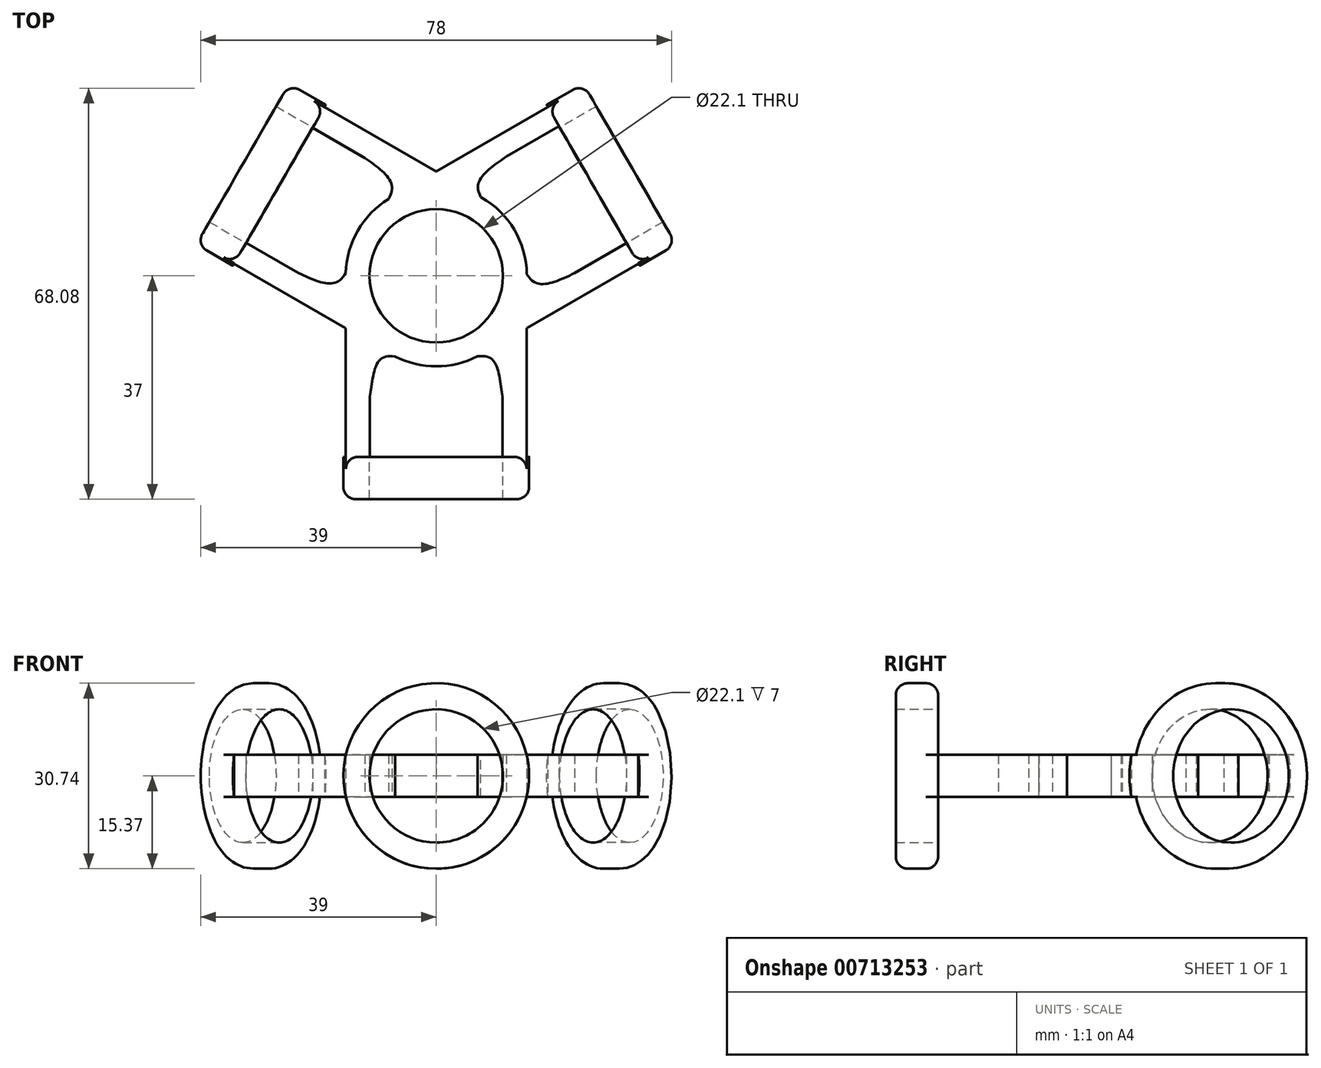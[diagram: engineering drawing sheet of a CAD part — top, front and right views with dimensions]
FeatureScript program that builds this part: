
annotation { "Feature Type Name" : "Feature", "Feature Type Description" : "" }
export const myFeature = defineFeature(function(context is Context, id is Id, definition is map)
    precondition{}
    {
        {
            var Q0;
            Q0=qCreatedBy(makeId("Top.planeOp"),FACE);
            var sketch = newSketch(context, id + "F0", { "sketchPlane" : qUnion([Q0])});
            skCircle(sketch, "E0", {"center": v(0, 0) * mm, "radius": 11.05 * mm});
            skCircle(sketch, "E1", {"center": v(0, 0) * mm, "radius": 15 * mm});
            skLineSegment(sketch, "E2", {"start": v(0, 0) * mm, "end": v(0, -30) * mm, "construction": true});
            skLineSegment(sketch, "E3", {"start": v(0, 0) * mm, "end": v(-25.98, 15) * mm, "construction": true});
            skLineSegment(sketch, "E4", {"start": v(0, 0) * mm, "end": v(25.98, 15) * mm, "construction": true});
            skLineSegment(sketch, "E5", {"start": v(0, 0) * mm, "end": v(7.5, -13) * mm, "construction": true});
            skLineSegment(sketch, "E6", {"start": v(0, -30) * mm, "end": v(-15, -30) * mm, "construction": true});
            skLineSegment(sketch, "E7", {"start": v(0, -30) * mm, "end": v(15, -30) * mm, "construction": true});
            skLineSegment(sketch, "E8", {"start": v(-33.48, 2) * mm, "end": v(-25.98, 15) * mm, "construction": true});
            skLineSegment(sketch, "E9", {"start": v(-18.48, 28) * mm, "end": v(-25.98, 15) * mm, "construction": true});
            skLineSegment(sketch, "E10", {"start": v(18.48, 28) * mm, "end": v(25.98, 15) * mm, "construction": true});
            skLineSegment(sketch, "E11", {"start": v(33.48, 2) * mm, "end": v(25.98, 15) * mm, "construction": true});
            skLineSegment(sketch, "E12", {"start": v(-15, -30) * mm, "end": v(-11, -30) * mm});
            skLineSegment(sketch, "E13", {"start": v(11, -30) * mm, "end": v(15, -30) * mm});
            skLineSegment(sketch, "E14", {"start": v(31.51, 5.42) * mm, "end": v(33.48, 2) * mm});
            skLineSegment(sketch, "E15", {"start": v(18.48, 28) * mm, "end": v(20.33, 24.79) * mm});
            skLineSegment(sketch, "E16", {"start": v(-20.48, 24.53) * mm, "end": v(-18.48, 28) * mm});
            skLineSegment(sketch, "E17", {"start": v(-33.48, 2) * mm, "end": v(-31.48, 5.47) * mm});
            skLineSegment(sketch, "E18", {"start": v(-18.48, 28) * mm, "end": v(7.5, 13) * mm});
            skLineSegment(sketch, "E19", {"start": v(-33.48, 2) * mm, "end": v(-7.5, -13) * mm});
            skLineSegment(sketch, "E20", {"start": v(18.48, 28) * mm, "end": v(-7.5, 13) * mm});
            skLineSegment(sketch, "E21", {"start": v(33.48, 2) * mm, "end": v(7.5, -13) * mm});
            skLineSegment(sketch, "E22", {"start": v(-15, -30) * mm, "end": v(-15, 0) * mm});
            skLineSegment(sketch, "E23", {"start": v(15, -30) * mm, "end": v(15, 0) * mm});
            skLineSegment(sketch, "E24", {"start": v(-11, -30) * mm, "end": v(-11, -10.2) * mm});
            skLineSegment(sketch, "E25", {"start": v(11, -30) * mm, "end": v(11, -10.2) * mm});
            skLineSegment(sketch, "E26", {"start": v(31.51, 5.42) * mm, "end": v(14.3, -4.51) * mm});
            skLineSegment(sketch, "E27", {"start": v(20.33, 24.79) * mm, "end": v(2.9, 14.72) * mm});
            skLineSegment(sketch, "E28", {"start": v(-31.48, 5.47) * mm, "end": v(-14.33, -4.43) * mm});
            skLineSegment(sketch, "E29", {"start": v(-20.48, 24.53) * mm, "end": v(-3.33, 14.63) * mm});
            skLineSegment(sketch, "E30", {"start": v(-22.82, 0.47) * mm, "end": v(-11.82, 19.53) * mm, "construction": true});
            skLineSegment(sketch, "E31", {"start": v(11.61, 19.75) * mm, "end": v(22.9, 0.46) * mm, "construction": true});
            skLineSegment(sketch, "E32", {"start": v(-11, -20) * mm, "end": v(11, -20) * mm, "construction": true});
            skFitSpline(sketch, "E33", {"points": [v(-11, -20) * mm, v(-9, -13.66) * mm, v(0, -15) * mm], "startDerivative": vector(2.85, 13.3) * mm, "endDerivative": vector(18.5, -2.63) * mm});
            skFitSpline(sketch, "E34", {"points": [v(11, -20) * mm, v(9, -13.66) * mm, v(0, -15) * mm], "startDerivative": vector(-2.93, 13.77) * mm, "endDerivative": vector(-18.48, -3.13) * mm});
            skLineSegment(sketch, "E35", {"start": v(-3.33, 14.63) * mm, "end": v(-7.33, 14.63) * mm, "construction": true});
            skLineSegment(sketch, "E36", {"start": v(2.9, 14.72) * mm, "end": v(6.9, 14.72) * mm, "construction": true});
            skLineSegment(sketch, "E37", {"start": v(-11, -10.2) * mm, "end": v(-9, -13.66) * mm, "construction": true});
            skLineSegment(sketch, "E38", {"start": v(0, 0) * mm, "end": v(-7.5, -13) * mm, "construction": true});
            skLineSegment(sketch, "E39", {"start": v(9, -13.66) * mm, "end": v(11, -10.2) * mm, "construction": true});
            skLineSegment(sketch, "E40", {"start": v(0, 0) * mm, "end": v(-7.5, 13) * mm, "construction": true});
            skLineSegment(sketch, "E41", {"start": v(-14.33, -4.43) * mm, "end": v(-16.33, -0.96) * mm, "construction": true});
            skLineSegment(sketch, "E42", {"start": v(14.3, -4.51) * mm, "end": v(16.3, -1.07) * mm, "construction": true});
            skLineSegment(sketch, "E43", {"start": v(-0.13, -0.22) * mm, "end": v(7.5, 13) * mm, "construction": true});
            skFitSpline(sketch, "E44", {"points": [v(-22.82, 0.47) * mm, v(-16.33, -0.96) * mm, v(-13, 7.5) * mm], "startDerivative": vector(15.9, -7.45) * mm, "endDerivative": vector(4.07, 20.77) * mm});
            skFitSpline(sketch, "E45", {"points": [v(-11.82, 19.53) * mm, v(-7.33, 14.63) * mm, v(-13, 7.5) * mm], "startDerivative": vector(14.4, -10.04) * mm, "endDerivative": vector(-15.95, -13.91) * mm});
            skFitSpline(sketch, "E46", {"points": [v(11.61, 19.75) * mm, v(6.9, 14.72) * mm, v(13, 7.5) * mm], "startDerivative": vector(-15.2, -10.36) * mm, "endDerivative": vector(17.12, -14.05) * mm});
            skFitSpline(sketch, "E47", {"points": [v(22.9, 0.46) * mm, v(16.3, -1.07) * mm, v(13, 7.5) * mm], "startDerivative": vector(-16.2, -7.76) * mm, "endDerivative": vector(-3.94, 21.12) * mm});
            skSolve(sketch);
        }
        {
            var Q0;
            Q0 = qSketchRegion(id + "F0", true);
            extrude(context, id + "F1", {"entities" : qUnion([Q0]), "depth" : 7 * mm, "offsetDistance" : 25 * mm});
        }
        {
            var Q0;
            Q0=makeQuery(id+"F1.opExtrude","SWEPT_FACE",FACE,{"disambiguationData":[OSD([sQuery(id+"F0.wireOp",EDGE,"E13")])]});
            var sketch = newSketch(context, id + "F2", { "sketchPlane" : qUnion([Q0])});
            skLineSegment(sketch, "E48", {"start": v(0, 0) * mm, "end": v(0, 3.5) * mm, "construction": true});
            skCircle(sketch, "E49", {"center": v(0, 3.5) * mm, "radius": 11.05 * mm});
            skCircle(sketch, "E50", {"center": v(0, 3.5) * mm, "radius": 15.37 * mm});
            skSolve(sketch);
        }
        {
            var Q0;
            Q0 = qSketchRegion(id + "F2", true);
            extrude(context, id + "F3", {"entities" : qUnion([Q0]), "operationType" : NewBodyOperationType.ADD, "depth" : 7 * mm, "offsetDistance" : 25 * mm});
        }
        {
            var Q0;
            Q0=makeQuery(id+"F1.opExtrude","SWEPT_FACE",FACE,{"disambiguationData":[OSD([sQuery(id+"F0.wireOp",EDGE,"E17")])]});
            var sketch = newSketch(context, id + "F4", { "sketchPlane" : qUnion([Q0])});
            skLineSegment(sketch, "E51", {"start": v(0, 0) * mm, "end": v(0, 3.5) * mm, "construction": true});
            skCircle(sketch, "E52", {"center": v(0, 3.5) * mm, "radius": 11.05 * mm});
            skCircle(sketch, "E53", {"center": v(0, 3.5) * mm, "radius": 15.37 * mm});
            skSolve(sketch);
        }
        {
            var Q0;
            Q0 = qSketchRegion(id + "F4", true);
            extrude(context, id + "F5", {"entities" : qUnion([Q0]), "operationType" : NewBodyOperationType.ADD, "depth" : 7 * mm, "offsetDistance" : 25 * mm});
        }
        {
            var Q0;
            Q0=makeQuery(id+"F1.opExtrude","SWEPT_FACE",FACE,{"disambiguationData":[OSD([sQuery(id+"F0.wireOp",EDGE,"E15")])]});
            var sketch = newSketch(context, id + "F6", { "sketchPlane" : qUnion([Q0])});
            skLineSegment(sketch, "E54", {"start": v(0, 0) * mm, "end": v(0, 3.5) * mm, "construction": true});
            skCircle(sketch, "E55", {"center": v(0, 3.5) * mm, "radius": 11.05 * mm});
            skCircle(sketch, "E56", {"center": v(0, 3.5) * mm, "radius": 15.37 * mm});
            skSolve(sketch);
        }
        {
            var Q0;
            Q0 = qSketchRegion(id + "F6", true);
            extrude(context, id + "F7", {"entities" : qUnion([Q0]), "operationType" : NewBodyOperationType.ADD, "depth" : 7 * mm, "offsetDistance" : 25 * mm});
        }
        {
            var Q0;
            {var subQ0=sQuery(id+"F0.wireOp",EDGE,"M36BIH5r-HAUe-k9cw-Y8AN-n1bEUGcGn69A");Q0=makeQuery(id+"F1.opExtrude","CAP_EDGE",EDGE,{"disambiguationData":[OSD([subQ0]),TDD([makeQuery(id+"F0.imprint","IMPRINT",EDGE,{"disambiguationData":[TD([[makeQuery(id+"F0.imprint","INTERSECT",VERTEX,{"derivedFrom":[subQ0,sQuery(id+"F0.wireOp",EDGE,"E17")]}),-1.0]])],"derivedFrom":subQ0})])],"isStart":false});}
            var Q1;
            {var subQ0=sQuery(id+"F0.wireOp",EDGE,"BCidmaKO-JP6u-Ivkp-FLMH-IQCRB2LKm121");Q1=makeQuery(id+"F1.opExtrude","CAP_EDGE",EDGE,{"disambiguationData":[OSD([subQ0]),TDD([makeQuery(id+"F0.imprint","IMPRINT",EDGE,{"disambiguationData":[TD([[makeQuery(id+"F0.imprint","INTERSECT",VERTEX,{"derivedFrom":[subQ0,sQuery(id+"F0.wireOp",EDGE,"E16")]}),-1.0]])],"derivedFrom":subQ0})])],"isStart":false});}
            var Q2;
            {var subQ0=sQuery(id+"F0.wireOp",EDGE,"lp6IFI2F-ik4T-MF6x-9fN9-Xrn4K0irZbfQ");Q2=makeQuery(id+"F1.opExtrude","CAP_EDGE",EDGE,{"disambiguationData":[OSD([subQ0]),TDD([makeQuery(id+"F0.imprint","IMPRINT",EDGE,{"disambiguationData":[TD([[makeQuery(id+"F0.imprint","INTERSECT",VERTEX,{"derivedFrom":[subQ0,sQuery(id+"F0.wireOp",EDGE,"E15")]}),-1.0]])],"derivedFrom":subQ0})])],"isStart":false});}
            var Q3;
            {var subQ0=sQuery(id+"F0.wireOp",EDGE,"ELQnSAp0-Pafx-ul33-bJbq-gA5hsUOoMWmb");Q3=makeQuery(id+"F1.opExtrude","CAP_EDGE",EDGE,{"disambiguationData":[OSD([subQ0]),TDD([makeQuery(id+"F0.imprint","IMPRINT",EDGE,{"disambiguationData":[TD([[makeQuery(id+"F0.imprint","INTERSECT",VERTEX,{"derivedFrom":[subQ0,sQuery(id+"F0.wireOp",EDGE,"E14")]}),-1.0]])],"derivedFrom":subQ0})])],"isStart":false});}
            var Q4;
            {var subQ0=sQuery(id+"F0.wireOp",EDGE,"Rb86YKMy-m54r-hE0W-wiJ9-LWPDYXBjSwaC");Q4=makeQuery(id+"F1.opExtrude","CAP_EDGE",EDGE,{"disambiguationData":[OSD([subQ0]),TDD([makeQuery(id+"F0.imprint","IMPRINT",EDGE,{"disambiguationData":[TD([[makeQuery(id+"F0.imprint","INTERSECT",VERTEX,{"derivedFrom":[subQ0,sQuery(id+"F0.wireOp",EDGE,"E13")]}),-1.0]])],"derivedFrom":subQ0})])],"isStart":false});}
            var Q5;
            {var subQ0=sQuery(id+"F0.wireOp",EDGE,"FxYZINIX-OOwV-yyRV-FRkK-c2HcUoVdKEcg");Q5=makeQuery(id+"F1.opExtrude","CAP_EDGE",EDGE,{"disambiguationData":[OSD([subQ0]),TDD([makeQuery(id+"F0.imprint","IMPRINT",EDGE,{"disambiguationData":[TD([[makeQuery(id+"F0.imprint","INTERSECT",VERTEX,{"derivedFrom":[subQ0,sQuery(id+"F0.wireOp",EDGE,"E12")]}),-1.0]])],"derivedFrom":subQ0})])],"isStart":false});}
            var Q6;
            {var subQ0=sQuery(id+"F0.wireOp",EDGE,"Rb86YKMy-m54r-hE0W-wiJ9-LWPDYXBjSwaC");Q6=makeQuery(id+"F1.opExtrude","CAP_EDGE",EDGE,{"disambiguationData":[OSD([subQ0]),TDD([makeQuery(id+"F0.imprint","IMPRINT",EDGE,{"disambiguationData":[TD([[makeQuery(id+"F0.imprint","INTERSECT",VERTEX,{"derivedFrom":[subQ0,sQuery(id+"F0.wireOp",EDGE,"E13")]}),-1.0]])],"derivedFrom":subQ0})])],"isStart":true});}
            var Q7;
            {var subQ0=sQuery(id+"F0.wireOp",EDGE,"ELQnSAp0-Pafx-ul33-bJbq-gA5hsUOoMWmb");Q7=makeQuery(id+"F1.opExtrude","CAP_EDGE",EDGE,{"disambiguationData":[OSD([subQ0]),TDD([makeQuery(id+"F0.imprint","IMPRINT",EDGE,{"disambiguationData":[TD([[makeQuery(id+"F0.imprint","INTERSECT",VERTEX,{"derivedFrom":[subQ0,sQuery(id+"F0.wireOp",EDGE,"E14")]}),-1.0]])],"derivedFrom":subQ0})])],"isStart":true});}
            var Q8;
            {var subQ0=sQuery(id+"F0.wireOp",EDGE,"lp6IFI2F-ik4T-MF6x-9fN9-Xrn4K0irZbfQ");Q8=makeQuery(id+"F1.opExtrude","CAP_EDGE",EDGE,{"disambiguationData":[OSD([subQ0]),TDD([makeQuery(id+"F0.imprint","IMPRINT",EDGE,{"disambiguationData":[TD([[makeQuery(id+"F0.imprint","INTERSECT",VERTEX,{"derivedFrom":[subQ0,sQuery(id+"F0.wireOp",EDGE,"E15")]}),-1.0]])],"derivedFrom":subQ0})])],"isStart":true});}
            var Q9;
            {var subQ0=sQuery(id+"F0.wireOp",EDGE,"BCidmaKO-JP6u-Ivkp-FLMH-IQCRB2LKm121");Q9=makeQuery(id+"F1.opExtrude","CAP_EDGE",EDGE,{"disambiguationData":[OSD([subQ0]),TDD([makeQuery(id+"F0.imprint","IMPRINT",EDGE,{"disambiguationData":[TD([[makeQuery(id+"F0.imprint","INTERSECT",VERTEX,{"derivedFrom":[subQ0,sQuery(id+"F0.wireOp",EDGE,"E16")]}),-1.0]])],"derivedFrom":subQ0})])],"isStart":true});}
            var Q10;
            {var subQ0=sQuery(id+"F0.wireOp",EDGE,"M36BIH5r-HAUe-k9cw-Y8AN-n1bEUGcGn69A");Q10=makeQuery(id+"F1.opExtrude","CAP_EDGE",EDGE,{"disambiguationData":[OSD([subQ0]),TDD([makeQuery(id+"F0.imprint","IMPRINT",EDGE,{"disambiguationData":[TD([[makeQuery(id+"F0.imprint","INTERSECT",VERTEX,{"derivedFrom":[subQ0,sQuery(id+"F0.wireOp",EDGE,"E17")]}),-1.0]])],"derivedFrom":subQ0})])],"isStart":true});}
            var Q11;
            {var subQ0=sQuery(id+"F0.wireOp",EDGE,"FxYZINIX-OOwV-yyRV-FRkK-c2HcUoVdKEcg");Q11=makeQuery(id+"F1.opExtrude","CAP_EDGE",EDGE,{"disambiguationData":[OSD([subQ0]),TDD([makeQuery(id+"F0.imprint","IMPRINT",EDGE,{"disambiguationData":[TD([[makeQuery(id+"F0.imprint","INTERSECT",VERTEX,{"derivedFrom":[subQ0,sQuery(id+"F0.wireOp",EDGE,"E12")]}),-1.0]])],"derivedFrom":subQ0})])],"isStart":true});}
            var Q12;
            Q12=makeQuery(id+"F7.opExtrude","CAP_EDGE",EDGE,{"disambiguationData":[OSD([sQuery(id+"F6.wireOp",EDGE,"E56")])],"isStart":false});
            var Q13;
            Q13=makeQuery(id+"F3.opExtrude","CAP_EDGE",EDGE,{"disambiguationData":[OSD([sQuery(id+"F2.wireOp",EDGE,"E50")])],"isStart":false});
            var Q14;
            Q14=makeQuery(id+"F5.opExtrude","CAP_EDGE",EDGE,{"disambiguationData":[OSD([sQuery(id+"F4.wireOp",EDGE,"E53")])],"isStart":false});
            fillet(context, id + "F8", {"entities" : qUnion([Q0, Q1, Q2, Q3, Q4, Q5, Q6, Q7, Q8, Q9, Q10, Q11, Q12, Q13, Q14]), "radius" : 2 * mm, "tangentPropagation" : true, "allowEdgeOverflow" : false});
        }
        {
            var Q0;
            {var subQ0=sQuery(id+"F0.wireOp",EDGE,"E13");var subQ2=sQuery(id+"F2.wireOp",EDGE,"E50");var subQ3=makeQuery(id+"F3.opExtrude","CAP_FACE",FACE,{"disambiguationData":[OSD([sQuery(id+"F2.wireOp",EDGE,"E49"),subQ2])],"isStart":true});var subQ4=sQuery(id+"F0.wireOp",EDGE,"E12");var subQ6=sQuery(id+"F0.wireOp",EDGE,"E17");var subQ7=sQuery(id+"F0.wireOp",EDGE,"E16");var subQ8=sQuery(id+"F0.wireOp",EDGE,"E15");var subQ9=sQuery(id+"F0.wireOp",EDGE,"E14");var subQ10=sQuery(id+"F0.wireOp",EDGE,"yFMh2vSi-dESU-roSY-NlWJ-D2NnP62kJ6aZ");var subQ11=sQuery(id+"F0.wireOp",EDGE,"MxBJSyvS-Fmrp-042r-ySUE-HMpYeUpcr8Ry");var subQ12=sQuery(id+"F0.wireOp",EDGE,"cHBSjouM-ive9-fqb4-oQAG-pubF9SUR5cwU");var subQ13=sQuery(id+"F0.wireOp",EDGE,"rupdORs6-A4il-8cmi-DNMe-a3LxSKAeor8D");var subQ14=sQuery(id+"F0.wireOp",EDGE,"dYG0iTOq-gft9-4OFM-1PV2-ACBu23Gv7qJD");var subQ15=sQuery(id+"F0.wireOp",EDGE,"M8sEbQj8-NoZn-PTSG-Y4XU-dObeHGLnaSbQ");var subQ16=sQuery(id+"F0.wireOp",EDGE,"lp6IFI2F-ik4T-MF6x-9fN9-Xrn4K0irZbfQ");var subQ17=sQuery(id+"F0.wireOp",EDGE,"BCidmaKO-JP6u-Ivkp-FLMH-IQCRB2LKm121");var subQ18=sQuery(id+"F0.wireOp",EDGE,"ELQnSAp0-Pafx-ul33-bJbq-gA5hsUOoMWmb");var subQ19=sQuery(id+"F0.wireOp",EDGE,"Rb86YKMy-m54r-hE0W-wiJ9-LWPDYXBjSwaC");var subQ20=sQuery(id+"F0.wireOp",EDGE,"FxYZINIX-OOwV-yyRV-FRkK-c2HcUoVdKEcg");var subQ21=sQuery(id+"F0.wireOp",EDGE,"M36BIH5r-HAUe-k9cw-Y8AN-n1bEUGcGn69A");var subQ22=sQuery(id+"F0.wireOp",EDGE,"E1");var subQ23=sQuery(id+"F0.wireOp",EDGE,"E0");var subQ24=makeQuery(id+"F3.opExtrude","SWEPT_FACE",FACE,{"disambiguationData":[OSD([subQ2])]});var subQ25=makeQuery(id+"F3.opExtrude","CAP_EDGE",EDGE,{"disambiguationData":[OSD([subQ2])],"isStart":true});Q0=makeQuery(id+"F8.opFillet","MERGE",EDGE,{"derivedFrom":[makeQuery(id+"F3.boolean.opBoolean","SPLIT",EDGE,{"disambiguationData":[topologyDisambiguationEdgeConnected([subQ3,subQ24]),TD([makeQuery(id+"F1.opExtrude","SWEPT_FACE",FACE,{"disambiguationData":[OSD([subQ20]),TDD([makeQuery(id+"F0.imprint","IMPRINT",EDGE,{"disambiguationData":[TD([[makeQuery(id+"F0.imprint","INTERSECT",VERTEX,{"derivedFrom":[subQ20,subQ4]}),-1.0]])],"derivedFrom":subQ20})])]})])],"derivedFrom":subQ25}),makeQuery(id+"F3.boolean.opBoolean","SPLIT",EDGE,{"disambiguationData":[topologyDisambiguationEdgeConnected([subQ3,subQ24]),TD([makeQuery(id+"F1.opExtrude","SWEPT_FACE",FACE,{"disambiguationData":[OSD([subQ19]),TDD([makeQuery(id+"F0.imprint","IMPRINT",EDGE,{"disambiguationData":[TD([[makeQuery(id+"F0.imprint","INTERSECT",VERTEX,{"derivedFrom":[subQ19,subQ0]}),-1.0]])],"derivedFrom":subQ19})])]})])],"derivedFrom":subQ25}),makeQuery(id+"F3.boolean.opBoolean","SPLIT",EDGE,{"disambiguationData":[topologyDisambiguationEdgeConnected([subQ3,subQ24]),TD([makeQuery(id+"F1.opExtrude","CAP_FACE",FACE,{"disambiguationData":[OSD([subQ23,subQ22,subQ21,subQ20,subQ19,subQ18,subQ17,subQ16,subQ15,subQ14,subQ13,subQ12,subQ11,subQ10,subQ4,subQ0,subQ9,subQ8,subQ7,subQ6])],"isStart":true})])],"derivedFrom":subQ25}),makeQuery(id+"F3.boolean.opBoolean","SPLIT",EDGE,{"disambiguationData":[topologyDisambiguationEdgeConnected([subQ3,subQ24]),TD([makeQuery(id+"F1.opExtrude","CAP_FACE",FACE,{"disambiguationData":[OSD([subQ23,subQ22,subQ21,subQ20,subQ19,subQ18,subQ17,subQ16,subQ15,subQ14,subQ13,subQ12,subQ11,subQ10,subQ4,subQ0,subQ9,subQ8,subQ7,subQ6])],"isStart":false})])],"derivedFrom":subQ25})]});}
            var Q1;
            {var subQ0=sQuery(id+"F0.wireOp",EDGE,"E14");var subQ2=sQuery(id+"F6.wireOp",EDGE,"E56");var subQ3=makeQuery(id+"F7.opExtrude","CAP_FACE",FACE,{"disambiguationData":[OSD([sQuery(id+"F6.wireOp",EDGE,"E55"),subQ2])],"isStart":true});var subQ4=sQuery(id+"F0.wireOp",EDGE,"E15");var subQ6=sQuery(id+"F0.wireOp",EDGE,"E17");var subQ7=sQuery(id+"F0.wireOp",EDGE,"E16");var subQ8=sQuery(id+"F0.wireOp",EDGE,"E13");var subQ9=sQuery(id+"F0.wireOp",EDGE,"E12");var subQ10=sQuery(id+"F0.wireOp",EDGE,"yFMh2vSi-dESU-roSY-NlWJ-D2NnP62kJ6aZ");var subQ11=sQuery(id+"F0.wireOp",EDGE,"MxBJSyvS-Fmrp-042r-ySUE-HMpYeUpcr8Ry");var subQ12=sQuery(id+"F0.wireOp",EDGE,"cHBSjouM-ive9-fqb4-oQAG-pubF9SUR5cwU");var subQ13=sQuery(id+"F0.wireOp",EDGE,"rupdORs6-A4il-8cmi-DNMe-a3LxSKAeor8D");var subQ14=sQuery(id+"F0.wireOp",EDGE,"dYG0iTOq-gft9-4OFM-1PV2-ACBu23Gv7qJD");var subQ15=sQuery(id+"F0.wireOp",EDGE,"M8sEbQj8-NoZn-PTSG-Y4XU-dObeHGLnaSbQ");var subQ16=sQuery(id+"F0.wireOp",EDGE,"lp6IFI2F-ik4T-MF6x-9fN9-Xrn4K0irZbfQ");var subQ17=sQuery(id+"F0.wireOp",EDGE,"BCidmaKO-JP6u-Ivkp-FLMH-IQCRB2LKm121");var subQ18=sQuery(id+"F0.wireOp",EDGE,"ELQnSAp0-Pafx-ul33-bJbq-gA5hsUOoMWmb");var subQ19=sQuery(id+"F0.wireOp",EDGE,"Rb86YKMy-m54r-hE0W-wiJ9-LWPDYXBjSwaC");var subQ20=sQuery(id+"F0.wireOp",EDGE,"FxYZINIX-OOwV-yyRV-FRkK-c2HcUoVdKEcg");var subQ21=sQuery(id+"F0.wireOp",EDGE,"M36BIH5r-HAUe-k9cw-Y8AN-n1bEUGcGn69A");var subQ22=sQuery(id+"F0.wireOp",EDGE,"E1");var subQ23=sQuery(id+"F0.wireOp",EDGE,"E0");var subQ24=makeQuery(id+"F7.opExtrude","SWEPT_FACE",FACE,{"disambiguationData":[OSD([subQ2])]});var subQ25=makeQuery(id+"F7.opExtrude","CAP_EDGE",EDGE,{"disambiguationData":[OSD([subQ2])],"isStart":true});Q1=makeQuery(id+"F8.opFillet","MERGE",EDGE,{"derivedFrom":[makeQuery(id+"F7.boolean.opBoolean","SPLIT",EDGE,{"disambiguationData":[topologyDisambiguationEdgeConnected([subQ3,subQ24]),TD([makeQuery(id+"F1.opExtrude","SWEPT_FACE",FACE,{"disambiguationData":[OSD([subQ18]),TDD([makeQuery(id+"F0.imprint","IMPRINT",EDGE,{"disambiguationData":[TD([[makeQuery(id+"F0.imprint","INTERSECT",VERTEX,{"derivedFrom":[subQ18,subQ0]}),-1.0]])],"derivedFrom":subQ18})])]})])],"derivedFrom":subQ25}),makeQuery(id+"F7.boolean.opBoolean","SPLIT",EDGE,{"disambiguationData":[topologyDisambiguationEdgeConnected([subQ3,subQ24]),TD([makeQuery(id+"F1.opExtrude","SWEPT_FACE",FACE,{"disambiguationData":[OSD([subQ16]),TDD([makeQuery(id+"F0.imprint","IMPRINT",EDGE,{"disambiguationData":[TD([[makeQuery(id+"F0.imprint","INTERSECT",VERTEX,{"derivedFrom":[subQ16,subQ4]}),-1.0]])],"derivedFrom":subQ16})])]})])],"derivedFrom":subQ25}),makeQuery(id+"F7.boolean.opBoolean","SPLIT",EDGE,{"disambiguationData":[topologyDisambiguationEdgeConnected([subQ3,subQ24]),TD([makeQuery(id+"F1.opExtrude","CAP_FACE",FACE,{"disambiguationData":[OSD([subQ23,subQ22,subQ21,subQ20,subQ19,subQ18,subQ17,subQ16,subQ15,subQ14,subQ13,subQ12,subQ11,subQ10,subQ9,subQ8,subQ0,subQ4,subQ7,subQ6])],"isStart":true})])],"derivedFrom":subQ25}),makeQuery(id+"F7.boolean.opBoolean","SPLIT",EDGE,{"disambiguationData":[topologyDisambiguationEdgeConnected([subQ3,subQ24]),TD([makeQuery(id+"F1.opExtrude","CAP_FACE",FACE,{"disambiguationData":[OSD([subQ23,subQ22,subQ21,subQ20,subQ19,subQ18,subQ17,subQ16,subQ15,subQ14,subQ13,subQ12,subQ11,subQ10,subQ9,subQ8,subQ0,subQ4,subQ7,subQ6])],"isStart":false})])],"derivedFrom":subQ25})]});}
            fillet(context, id + "F9", {"entities" : qUnion([Q0, Q1]), "radius" : 2 * mm, "tangentPropagation" : true, "allowEdgeOverflow" : false});
        }
        {
            var Q0;
            {var subQ0=sQuery(id+"F4.wireOp",EDGE,"E53");var subQ1=makeQuery(id+"F5.opExtrude","CAP_FACE",FACE,{"disambiguationData":[OSD([sQuery(id+"F4.wireOp",EDGE,"E52"),subQ0])],"isStart":true});var subQ2=sQuery(id+"F0.wireOp",EDGE,"E16");var subQ3=sQuery(id+"F0.wireOp",EDGE,"E17");var subQ4=makeQuery(id+"F5.opExtrude","SWEPT_FACE",FACE,{"disambiguationData":[OSD([subQ0])]});Q0=makeQuery(id+"F5.boolean.opBoolean","SPLIT",EDGE,{"disambiguationData":[topologyDisambiguationEdgeConnected([subQ1,subQ4]),TD([makeQuery(id+"F1.opExtrude","CAP_FACE",FACE,{"disambiguationData":[OSD([sQuery(id+"F0.wireOp",EDGE,"E0"),sQuery(id+"F0.wireOp",EDGE,"E1"),sQuery(id+"F0.wireOp",EDGE,"E12"),sQuery(id+"F0.wireOp",EDGE,"E13"),sQuery(id+"F0.wireOp",EDGE,"E14"),sQuery(id+"F0.wireOp",EDGE,"E15"),subQ2,subQ3,sQuery(id+"F0.wireOp",EDGE,"E18"),sQuery(id+"F0.wireOp",EDGE,"E19"),sQuery(id+"F0.wireOp",EDGE,"E20"),sQuery(id+"F0.wireOp",EDGE,"E21"),sQuery(id+"F0.wireOp",EDGE,"E22"),sQuery(id+"F0.wireOp",EDGE,"E23"),sQuery(id+"F0.wireOp",EDGE,"E24"),sQuery(id+"F0.wireOp",EDGE,"E25"),sQuery(id+"F0.wireOp",EDGE,"E26"),sQuery(id+"F0.wireOp",EDGE,"E27"),sQuery(id+"F0.wireOp",EDGE,"E28"),sQuery(id+"F0.wireOp",EDGE,"E29")])],"isStart":true})])],"derivedFrom":makeQuery(id+"F5.opExtrude","CAP_EDGE",EDGE,{"disambiguationData":[OSD([subQ0])],"isStart":true})});}
            var Q1;
            {var subQ0=sQuery(id+"F4.wireOp",EDGE,"E53");var subQ1=makeQuery(id+"F5.opExtrude","CAP_FACE",FACE,{"disambiguationData":[OSD([sQuery(id+"F4.wireOp",EDGE,"E52"),subQ0])],"isStart":true});var subQ2=sQuery(id+"F0.wireOp",EDGE,"E17");var subQ3=sQuery(id+"F0.wireOp",EDGE,"E16");var subQ4=makeQuery(id+"F5.opExtrude","SWEPT_FACE",FACE,{"disambiguationData":[OSD([subQ0])]});Q1=makeQuery(id+"F5.boolean.opBoolean","SPLIT",EDGE,{"disambiguationData":[topologyDisambiguationEdgeConnected([subQ1,subQ4]),TD([makeQuery(id+"F1.opExtrude","CAP_FACE",FACE,{"disambiguationData":[OSD([sQuery(id+"F0.wireOp",EDGE,"E0"),sQuery(id+"F0.wireOp",EDGE,"E1"),sQuery(id+"F0.wireOp",EDGE,"E12"),sQuery(id+"F0.wireOp",EDGE,"E13"),sQuery(id+"F0.wireOp",EDGE,"E14"),sQuery(id+"F0.wireOp",EDGE,"E15"),subQ3,subQ2,sQuery(id+"F0.wireOp",EDGE,"E18"),sQuery(id+"F0.wireOp",EDGE,"E19"),sQuery(id+"F0.wireOp",EDGE,"E20"),sQuery(id+"F0.wireOp",EDGE,"E21"),sQuery(id+"F0.wireOp",EDGE,"E22"),sQuery(id+"F0.wireOp",EDGE,"E23"),sQuery(id+"F0.wireOp",EDGE,"E24"),sQuery(id+"F0.wireOp",EDGE,"E25"),sQuery(id+"F0.wireOp",EDGE,"E26"),sQuery(id+"F0.wireOp",EDGE,"E27"),sQuery(id+"F0.wireOp",EDGE,"E28"),sQuery(id+"F0.wireOp",EDGE,"E29")])],"isStart":false})])],"derivedFrom":makeQuery(id+"F5.opExtrude","CAP_EDGE",EDGE,{"disambiguationData":[OSD([subQ0])],"isStart":true})});}
            fillet(context, id + "F10", {"entities" : qUnion([Q0, Q1]), "radius" : 2 * mm, "tangentPropagation" : true, "allowEdgeOverflow" : false});
        }
        {
            var Q0;
            {var subQ0=sQuery(id+"F0.wireOp",EDGE,"E19");var subQ1=sQuery(id+"F0.wireOp",EDGE,"E1");var subQ2=makeQuery(id+"F0.imprint","INTERSECT",VERTEX,{"derivedFrom":[subQ1,subQ0]});Q0=makeQuery(id+"F0.imprint","IMPRINT",FACE,{"disambiguationData":[TD([[makeQuery(id+"F0.imprint","IMPRINT",EDGE,{"disambiguationData":[TD([[subQ2,1.0]])],"derivedFrom":subQ1}),-1.0]])]});}
            extrude(context, id + "F11", {"entities" : qUnion([Q0]), "operationType" : NewBodyOperationType.ADD, "depth" : 7 * mm, "offsetDistance" : 25 * mm});
        }
        {
            var Q0;
            {var subQ0=sQuery(id+"F0.wireOp",EDGE,"E21");var subQ1=sQuery(id+"F0.wireOp",EDGE,"E1");var subQ2=makeQuery(id+"F0.imprint","INTERSECT",VERTEX,{"derivedFrom":[subQ1,subQ0]});Q0=makeQuery(id+"F0.imprint","IMPRINT",FACE,{"disambiguationData":[TD([[makeQuery(id+"F0.imprint","IMPRINT",EDGE,{"disambiguationData":[TD([[subQ2,-1.0]])],"derivedFrom":subQ1}),-1.0]])]});}
            extrude(context, id + "F12", {"entities" : qUnion([Q0]), "operationType" : NewBodyOperationType.ADD, "depth" : 7 * mm, "offsetDistance" : 25 * mm});
        }
        {
            var Q0;
            {var subQ0=sQuery(id+"F0.wireOp",EDGE,"E22");var subQ1=sQuery(id+"F0.wireOp",EDGE,"E1");var subQ2=makeQuery(id+"F0.imprint","INTERSECT",VERTEX,{"derivedFrom":[subQ1,subQ0]});Q0=makeQuery(id+"F0.imprint","IMPRINT",FACE,{"disambiguationData":[TD([[makeQuery(id+"F0.imprint","IMPRINT",EDGE,{"disambiguationData":[TD([[subQ2,-1.0]])],"derivedFrom":subQ1}),-1.0]])]});}
            extrude(context, id + "F13", {"entities" : qUnion([Q0]), "operationType" : NewBodyOperationType.ADD, "depth" : 7 * mm, "offsetDistance" : 25 * mm});
        }
        {
            var Q0;
            {var subQ0=sQuery(id+"F0.wireOp",EDGE,"E21");var subQ1=sQuery(id+"F0.wireOp",EDGE,"E1");var subQ2=makeQuery(id+"F0.imprint","INTERSECT",VERTEX,{"derivedFrom":[subQ1,subQ0]});Q0=makeQuery(id+"F0.imprint","IMPRINT",FACE,{"disambiguationData":[TD([[makeQuery(id+"F0.imprint","IMPRINT",EDGE,{"disambiguationData":[TD([[subQ2,-1.0]])],"derivedFrom":subQ1}),-1.0]])]});}
            var Q1;
            {var subQ0=sQuery(id+"F0.wireOp",EDGE,"E23");var subQ1=sQuery(id+"F0.wireOp",EDGE,"E1");var subQ2=makeQuery(id+"F0.imprint","INTERSECT",VERTEX,{"derivedFrom":[subQ1,subQ0]});Q1=makeQuery(id+"F0.imprint","IMPRINT",FACE,{"disambiguationData":[TD([[makeQuery(id+"F0.imprint","IMPRINT",EDGE,{"disambiguationData":[TD([[subQ2,1.0]])],"derivedFrom":subQ1}),-1.0]])]});}
            var Q2;
            {var subQ0=sQuery(id+"F0.wireOp",EDGE,"E27");var subQ1=sQuery(id+"F0.wireOp",EDGE,"E1");var subQ2=makeQuery(id+"F0.imprint","INTERSECT",VERTEX,{"derivedFrom":[subQ1,subQ0]});Q2=makeQuery(id+"F0.imprint","IMPRINT",FACE,{"disambiguationData":[TD([[makeQuery(id+"F0.imprint","IMPRINT",EDGE,{"disambiguationData":[TD([[subQ2,1.0]])],"derivedFrom":subQ1}),-1.0]])]});}
            var Q3;
            {var subQ0=sQuery(id+"F0.wireOp",EDGE,"E20");var subQ1=sQuery(id+"F0.wireOp",EDGE,"E1");var subQ2=makeQuery(id+"F0.imprint","INTERSECT",VERTEX,{"derivedFrom":[subQ1,subQ0]});Q3=makeQuery(id+"F0.imprint","IMPRINT",FACE,{"disambiguationData":[TD([[makeQuery(id+"F0.imprint","IMPRINT",EDGE,{"disambiguationData":[TD([[subQ2,1.0]])],"derivedFrom":subQ1}),-1.0]])]});}
            extrude(context, id + "F14", {"entities" : qUnion([Q0, Q1, Q2, Q3]), "operationType" : NewBodyOperationType.ADD, "depth" : 7 * mm, "offsetDistance" : 25 * mm});
        }
    });
